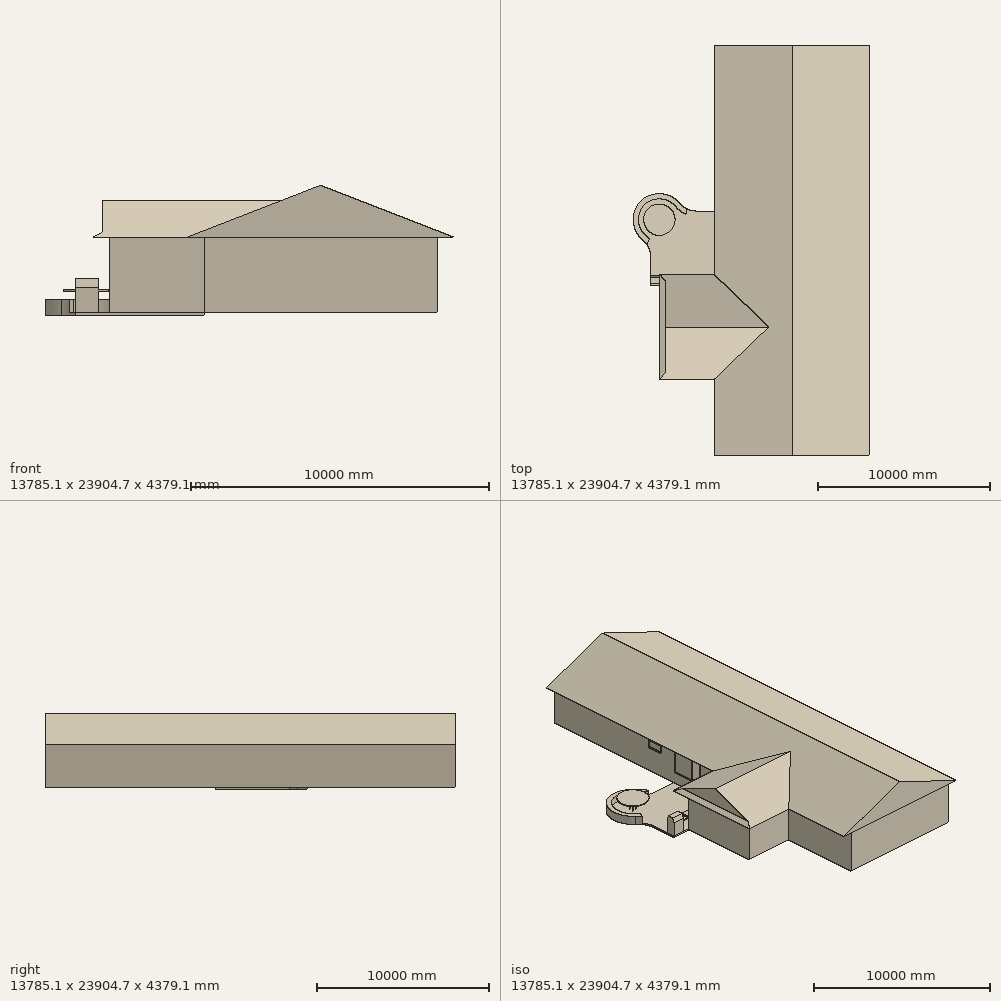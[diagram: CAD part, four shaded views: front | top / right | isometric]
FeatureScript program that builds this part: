
annotation { "Feature Type Name" : "Feature", "Feature Type Description" : "" }
export const myFeature = defineFeature(function(context is Context, id is Id, definition is map)
    precondition{}
    {
        {
            var Q0;
            Q0=qCreatedBy(makeId("Top.planeOp"),FACE);
            var sketch = newSketch(context, id + "F0", { "sketchPlane" : qUnion([Q0])});
            skLineSegment(sketch, "E0", {"start": v(0, 0) * mm, "end": v(-3175, 0) * mm});
            skLineSegment(sketch, "E1", {"start": v(-3175, 0) * mm, "end": v(-3175, -4902.2) * mm});
            skLineSegment(sketch, "E2", {"start": v(-3175, -4902.2) * mm, "end": v(0, -4902.2) * mm});
            skLineSegment(sketch, "E3", {"start": v(0, -4902.2) * mm, "end": v(0, -9934.69) * mm});
            skLineSegment(sketch, "E4", {"start": v(0, -9934.69) * mm, "end": v(7841.53, -9934.69) * mm});
            skLineSegment(sketch, "E5", {"start": v(7841.53, -9934.69) * mm, "end": v(7841.53, 13970) * mm});
            skLineSegment(sketch, "E6", {"start": v(7841.53, 13970) * mm, "end": v(0, 13970) * mm});
            skLineSegment(sketch, "E7", {"start": v(0, 13970) * mm, "end": v(0, 0) * mm});
            skSolve(sketch);
        }
        {
            var Q0;
            Q0 = qSketchRegion(id + "F0", true);
            extrude(context, id + "F1", {"entities" : qUnion([Q0]), "depth" : 2514.6 * mm, "offsetDistance" : 25.4 * mm});
        }
        {
            var Q0;
            Q0=qCreatedBy(makeId("Front.planeOp"),FACE);
            var sketch = newSketch(context, id + "F2", { "sketchPlane" : qUnion([Q0])});
            skLineSegment(sketch, "E8", {"start": v(8451.13, 2514.6) * mm, "end": v(-609.6, 2514.6) * mm});
            skLineSegment(sketch, "E9", {"start": v(-609.6, 2514.6) * mm, "end": v(3920.77, 4277.52) * mm});
            skLineSegment(sketch, "E10", {"start": v(3920.77, 4277.52) * mm, "end": v(8451.13, 2514.6) * mm});
            skSolve(sketch);
        }
        {
            var Q0;
            Q0=makeQuery(id+"F2.imprint","IMPRINT",FACE,{"disambiguationData":[TD([[makeQuery(id+"F2.imprint","IMPRINT",EDGE,{"derivedFrom":sQuery(id+"F2.wireOp",EDGE,"E8")}),-1.0]])]});
            var Q1;
            Q1=makeQuery(id+"F1.opExtrude","SWEPT_FACE",FACE,{"disambiguationData":[OSD([sQuery(id+"F0.wireOp",EDGE,"E6")])]});
            var Q2;
            Q2=makeQuery(id+"F1.opExtrude","SWEPT_FACE",FACE,{"disambiguationData":[OSD([sQuery(id+"F0.wireOp",EDGE,"E4")])]});
            extrude(context, id + "F3", {"entities" : qUnion([Q0]), "endBound" : BoundingType.UP_TO_SURFACE, "oppositeDirection" : true, "depth" : 25.4 * mm, "endBoundEntityFace" : qUnion([Q1]), "offsetDistance" : 25.4 * mm, "hasSecondDirection" : true, "secondDirectionBound" : SecondDirectionBoundingType.UP_TO_SURFACE, "secondDirectionOppositeDirection" : false, "secondDirectionDepth" : 25.4 * mm, "secondDirectionBoundEntityFace" : qUnion([Q2])});
        }
        {
            var Q0;
            Q0=makeQuery(id+"F1.opExtrude","SWEPT_FACE",FACE,{"disambiguationData":[OSD([sQuery(id+"F0.wireOp",EDGE,"E1")])]});
            var sketch = newSketch(context, id + "F4", { "sketchPlane" : qUnion([Q0])});
            skLineSegment(sketch, "E11", {"start": v(-609.6, 2514.6) * mm, "end": v(5511.8, 2514.6) * mm});
            skLineSegment(sketch, "E12", {"start": v(5511.8, 2514.6) * mm, "end": v(2451.1, 3758.26) * mm});
            skLineSegment(sketch, "E13", {"start": v(2451.1, 3758.26) * mm, "end": v(-609.6, 2514.6) * mm});
            skSolve(sketch);
        }
        {
            var Q0;
            {var subQ0=sQuery(id+"F4.wireOp",EDGE,"E12");Q0=makeQuery(id+"F4.imprint","IMPRINT",FACE,{"disambiguationData":[TD([[makeQuery(id+"F4.imprint","IMPRINT",EDGE,{"derivedFrom":subQ0}),1.0]])]});}
            extrude(context, id + "F5", {"entities" : qUnion([Q0]), "endBound" : BoundingType.UP_TO_NEXT, "oppositeDirection" : true, "depth" : 25.4 * mm, "offsetDistance" : 25.4 * mm, "hasSecondDirection" : true, "secondDirectionOppositeDirection" : false, "secondDirectionDepth" : 254 * mm});
        }
        {
            var Q0;
            Q0=makeQuery(id+"F1.opExtrude","SWEPT_FACE",FACE,{"disambiguationData":[OSD([sQuery(id+"F0.wireOp",EDGE,"E0")])]});
            var sketch = newSketch(context, id + "F6", { "sketchPlane" : qUnion([Q0])});
            skLineSegment(sketch, "E14", {"start": v(3429, 2514.6) * mm, "end": v(3784.6, 2514.6) * mm});
            skLineSegment(sketch, "E15", {"start": v(3784.6, 2514.6) * mm, "end": v(3429, 2682.87) * mm});
            skLineSegment(sketch, "E16", {"start": v(3429, 2682.87) * mm, "end": v(3429, 2514.6) * mm});
            skSolve(sketch);
        }
        {
            var Q0;
            Q0=makeQuery(id+"F6.imprint","IMPRINT",FACE,{"disambiguationData":[TD([[makeQuery(id+"F6.imprint","IMPRINT",EDGE,{"derivedFrom":sQuery(id+"F6.wireOp",EDGE,"E14")}),1.0]])]});
            var Q1;
            Q1=makeQuery(id+"F5.opExtrude","SWEPT_FACE",FACE,{"disambiguationData":[OSD([sQuery(id+"F4.wireOp",EDGE,"E13")])]});
            var Q2;
            Q2=makeQuery(id+"F5.opExtrude","SWEPT_FACE",FACE,{"disambiguationData":[OSD([sQuery(id+"F4.wireOp",EDGE,"E12")])]});
            extrude(context, id + "F7", {"entities" : qUnion([Q0]), "operationType" : NewBodyOperationType.ADD, "endBound" : BoundingType.UP_TO_SURFACE, "depth" : 25.4 * mm, "endBoundEntityFace" : qUnion([Q1]), "offsetDistance" : 25.4 * mm, "hasSecondDirection" : true, "secondDirectionBound" : SecondDirectionBoundingType.UP_TO_SURFACE, "secondDirectionOppositeDirection" : true, "secondDirectionDepth" : 25.4 * mm, "secondDirectionBoundEntityFace" : qUnion([Q2])});
        }
        {
            var Q0;
            Q0=makeQuery(id+"F1.opExtrude","SWEPT_FACE",FACE,{"disambiguationData":[OSD([sQuery(id+"F0.wireOp",EDGE,"E0")])]});
            var sketch = newSketch(context, id + "F8", { "sketchPlane" : qUnion([Q0])});
            skLineSegment(sketch, "E17.bottom", {"start": v(660.4, 2235.2) * mm, "end": v(2463.8, 2235.2) * mm});
            skLineSegment(sketch, "E17.top", {"start": v(660.4, 228.6) * mm, "end": v(2463.8, 228.6) * mm});
            skLineSegment(sketch, "E17.left", {"start": v(660.4, 2235.2) * mm, "end": v(660.4, 228.6) * mm});
            skLineSegment(sketch, "E18.right", {"start": v(2463.8, 2235.2) * mm, "end": v(2463.8, 228.6) * mm});
            skLineSegment(sketch, "E19.0", {"start": v(711.2, 2184.4) * mm, "end": v(1536.7, 2184.4) * mm});
            skLineSegment(sketch, "E19.1", {"start": v(711.2, 2184.4) * mm, "end": v(711.2, 279.4) * mm});
            skLineSegment(sketch, "E19.2", {"start": v(711.2, 279.4) * mm, "end": v(1536.7, 279.4) * mm});
            skLineSegment(sketch, "E19.3", {"start": v(1536.7, 2184.4) * mm, "end": v(1536.7, 279.4) * mm});
            skLineSegment(sketch, "E20.0", {"start": v(-6.35, -6.35) * mm, "end": v(3181.35, -6.35) * mm});
            skLineSegment(sketch, "E20.1", {"start": v(-6.35, 2520.95) * mm, "end": v(-6.35, -6.35) * mm});
            skLineSegment(sketch, "E20.2", {"start": v(3181.35, 2520.95) * mm, "end": v(-6.35, 2520.95) * mm});
            skLineSegment(sketch, "E20.3", {"start": v(3181.35, -6.35) * mm, "end": v(3181.35, 2520.95) * mm});
            skLineSegment(sketch, "E21.0", {"start": v(1587.5, 2184.4) * mm, "end": v(2413, 2184.4) * mm});
            skLineSegment(sketch, "E21.1", {"start": v(1587.5, 2184.4) * mm, "end": v(1587.5, 279.4) * mm});
            skLineSegment(sketch, "E21.2", {"start": v(1587.5, 279.4) * mm, "end": v(2413, 279.4) * mm});
            skLineSegment(sketch, "E21.3", {"start": v(2413, 2184.4) * mm, "end": v(2413, 279.4) * mm});
            skLineSegment(sketch, "E22", {"start": v(1562.1, 2298.82) * mm, "end": v(1562.1, -195.7) * mm, "construction": true});
            skSolve(sketch);
        }
        {
            var Q0;
            Q0=makeQuery(id+"F8.imprint","IMPRINT",FACE,{"disambiguationData":[TD([[makeQuery(id+"F8.imprint","IMPRINT",EDGE,{"derivedFrom":sQuery(id+"F8.wireOp",EDGE,"E17.bottom")}),-1.0]])]});
            var Q1;
            Q1=makeQuery(id+"F8.imprint","IMPRINT",FACE,{"disambiguationData":[TD([[makeQuery(id+"F8.imprint","IMPRINT",EDGE,{"derivedFrom":sQuery(id+"F8.wireOp",EDGE,"E18.bottom")}),-1.0]])]});
            extrude(context, id + "F9", {"entities" : qUnion([Q0, Q1]), "depth" : 25.4 * mm, "offsetDistance" : 25.4 * mm});
        }
        {
            var Q0;
            Q0=makeQuery(id+"F1.opExtrude","SWEPT_FACE",FACE,{"disambiguationData":[OSD([sQuery(id+"F0.wireOp",EDGE,"E0")])]});
            var sketch = newSketch(context, id + "F10", { "sketchPlane" : qUnion([Q0])});
            skLineSegment(sketch, "E23.0", {"start": v(711.2, 2184.4) * mm, "end": v(711.2, 279.4) * mm});
            skLineSegment(sketch, "E24.0", {"start": v(711.2, 2184.4) * mm, "end": v(1536.7, 2184.4) * mm});
            skLineSegment(sketch, "E25.0", {"start": v(1536.7, 2184.4) * mm, "end": v(1536.7, 279.4) * mm});
            skLineSegment(sketch, "E26.0", {"start": v(711.2, 279.4) * mm, "end": v(1536.7, 279.4) * mm});
            skLineSegment(sketch, "E27.0", {"start": v(1587.5, 2184.4) * mm, "end": v(1587.5, 279.4) * mm});
            skPoint(sketch, "E28.0", {"position": v(2000.25, 279.4) * mm});
            skLineSegment(sketch, "E29.0", {"start": v(2413, 2184.4) * mm, "end": v(2413, 279.4) * mm});
            skLineSegment(sketch, "E30.0", {"start": v(1587.5, 2184.4) * mm, "end": v(2413, 2184.4) * mm});
            skLineSegment(sketch, "E31", {"start": v(1587.5, 279.4) * mm, "end": v(2413, 279.4) * mm});
            skSolve(sketch);
        }
        {
            var Q0;
            Q0 = qSketchRegion(id + "F10", true);
            extrude(context, id + "F11", {"entities" : qUnion([Q0]), "depth" : 12.7 * mm, "offsetDistance" : 25.4 * mm});
        }
        {
            var Q0;
            Q0=makeQuery(id+"F1.opExtrude","SWEPT_FACE",FACE,{"disambiguationData":[OSD([sQuery(id+"F0.wireOp",EDGE,"E7")])]});
            var sketch = newSketch(context, id + "F12", { "sketchPlane" : qUnion([Q0])});
            skLineSegment(sketch, "E32.bottom", {"start": v(-1193.8, 2514.6) * mm, "end": v(-304.8, 2514.6) * mm});
            skLineSegment(sketch, "E32.top", {"start": v(-1193.8, 990.6) * mm, "end": v(-304.8, 990.6) * mm});
            skLineSegment(sketch, "E32.left", {"start": v(-1193.8, 2514.6) * mm, "end": v(-1193.8, 990.6) * mm});
            skLineSegment(sketch, "E32.right", {"start": v(-304.8, 2514.6) * mm, "end": v(-304.8, 990.6) * mm});
            skLineSegment(sketch, "E33.0", {"start": v(-1143, 2463.8) * mm, "end": v(-355.6, 2463.8) * mm});
            skLineSegment(sketch, "E33.1", {"start": v(-1143, 2463.8) * mm, "end": v(-1143, 1041.4) * mm});
            skLineSegment(sketch, "E33.2", {"start": v(-1143, 1041.4) * mm, "end": v(-355.6, 1041.4) * mm});
            skLineSegment(sketch, "E33.3", {"start": v(-355.6, 2463.8) * mm, "end": v(-355.6, 1041.4) * mm});
            skLineSegment(sketch, "E34.0", {"start": v(-13976.35, -6.35) * mm, "end": v(6.35, -6.35) * mm});
            skLineSegment(sketch, "E34.1", {"start": v(-13976.35, 2520.95) * mm, "end": v(-13976.35, -6.35) * mm});
            skLineSegment(sketch, "E34.2", {"start": v(6.35, 2520.95) * mm, "end": v(-13976.35, 2520.95) * mm});
            skLineSegment(sketch, "E34.3", {"start": v(6.35, -6.35) * mm, "end": v(6.35, 2520.95) * mm});
            skSolve(sketch);
        }
        {
            var Q0;
            Q0=makeQuery(id+"F12.imprint","IMPRINT",FACE,{"disambiguationData":[TD([[makeQuery(id+"F12.imprint","IMPRINT",EDGE,{"derivedFrom":sQuery(id+"F12.wireOp",EDGE,"E32.bottom")}),-1.0]])]});
            extrude(context, id + "F13", {"entities" : qUnion([Q0]), "depth" : 25.4 * mm, "offsetDistance" : 25.4 * mm});
        }
        {
            var Q0;
            Q0=makeQuery(id+"F1.opExtrude","SWEPT_FACE",FACE,{"disambiguationData":[OSD([sQuery(id+"F0.wireOp",EDGE,"E7")])]});
            var sketch = newSketch(context, id + "F14", { "sketchPlane" : qUnion([Q0])});
            skLineSegment(sketch, "E35.0", {"start": v(-355.6, 2463.8) * mm, "end": v(-355.6, 1041.4) * mm});
            skLineSegment(sketch, "E36.0", {"start": v(-1143, 2463.8) * mm, "end": v(-355.6, 2463.8) * mm});
            skLineSegment(sketch, "E37.0", {"start": v(-1143, 2463.8) * mm, "end": v(-1143, 1041.4) * mm});
            skLineSegment(sketch, "E38.0", {"start": v(-1143, 1041.4) * mm, "end": v(-355.6, 1041.4) * mm});
            skSolve(sketch);
        }
        {
            var Q0;
            Q0 = qSketchRegion(id + "F14", true);
            extrude(context, id + "F15", {"entities" : qUnion([Q0]), "depth" : 6.35 * mm, "offsetDistance" : 25.4 * mm});
        }
        {
            var Q0;
            Q0=makeQuery(id+"F3.opExtrude","SWEPT_FACE",FACE,{"disambiguationData":[OSD([sQuery(id+"F2.wireOp",EDGE,"E8")])]});
            var sketch = newSketch(context, id + "F16", { "sketchPlane" : qUnion([Q0])});
            skLineSegment(sketch, "E39", {"start": v(0, -2235.2) * mm, "end": v(0, -4089.4) * mm});
            skLineSegment(sketch, "E40", {"start": v(0, -4089.4) * mm, "end": v(-431.8, -3860.8) * mm});
            skLineSegment(sketch, "E41", {"start": v(-431.8, -3860.8) * mm, "end": v(-431.8, -2463.8) * mm});
            skLineSegment(sketch, "E42", {"start": v(-431.8, -2463.8) * mm, "end": v(0, -2235.2) * mm});
            skLineSegment(sketch, "E43", {"start": v(-431.8, -3162.3) * mm, "end": v(358.3, -3162.3) * mm, "construction": true});
            skSolve(sketch);
        }
        {
            var Q0;
            Q0=makeQuery(id+"F16.imprint","IMPRINT",FACE,{"disambiguationData":[TD([[makeQuery(id+"F16.imprint","IMPRINT",EDGE,{"derivedFrom":sQuery(id+"F16.wireOp",EDGE,"E39")}),-1.0]])]});
            extrude(context, id + "F17", {"entities" : qUnion([Q0]), "depth" : 1473.2 * mm, "offsetDistance" : 25.4 * mm});
        }
        {
            var Q0;
            Q0=makeQuery(id+"F17.opExtrude","SWEPT_FACE",FACE,{"disambiguationData":[OSD([sQuery(id+"F16.wireOp",EDGE,"E40")])]});
            var sketch = newSketch(context, id + "F18", { "sketchPlane" : qUnion([Q0])});
            skLineSegment(sketch, "E44.0", {"start": v(-1475.6, 2463.8) * mm, "end": v(-1862.58, 2463.8) * mm});
            skLineSegment(sketch, "E44.1", {"start": v(-1475.6, 1092.2) * mm, "end": v(-1475.6, 2463.8) * mm});
            skLineSegment(sketch, "E44.2", {"start": v(-1862.58, 1092.2) * mm, "end": v(-1475.6, 1092.2) * mm});
            skLineSegment(sketch, "E44.3", {"start": v(-1862.58, 2463.8) * mm, "end": v(-1862.58, 1092.2) * mm});
            skSolve(sketch);
        }
        {
            var Q0;
            Q0 = qSketchRegion(id + "F18", true);
            extrude(context, id + "F19", {"entities" : qUnion([Q0]), "operationType" : NewBodyOperationType.REMOVE, "oppositeDirection" : true, "depth" : 25.4 * mm, "offsetDistance" : 25.4 * mm});
        }
        {
            var Q0;
            Q0=makeQuery(id+"F17.opExtrude","SWEPT_FACE",FACE,{"disambiguationData":[OSD([sQuery(id+"F16.wireOp",EDGE,"E41")])]});
            var sketch = newSketch(context, id + "F20", { "sketchPlane" : qUnion([Q0])});
            skLineSegment(sketch, "E45.0", {"start": v(-2514.6, 2463.8) * mm, "end": v(-3810, 2463.8) * mm});
            skLineSegment(sketch, "E45.1", {"start": v(-2514.6, 1092.2) * mm, "end": v(-2514.6, 2463.8) * mm});
            skLineSegment(sketch, "E45.2", {"start": v(-3810, 1092.2) * mm, "end": v(-2514.6, 1092.2) * mm});
            skLineSegment(sketch, "E45.3", {"start": v(-3810, 2463.8) * mm, "end": v(-3810, 1092.2) * mm});
            skSolve(sketch);
        }
        {
            var Q0;
            Q0=makeQuery(id+"F20.imprint","IMPRINT",FACE,{"disambiguationData":[TD([[makeQuery(id+"F20.imprint","IMPRINT",EDGE,{"derivedFrom":sQuery(id+"F20.wireOp",EDGE,"E45.0")}),1.0]])]});
            extrude(context, id + "F21", {"entities" : qUnion([Q0]), "operationType" : NewBodyOperationType.REMOVE, "oppositeDirection" : true, "depth" : 25.4 * mm, "offsetDistance" : 25.4 * mm});
        }
        {
            var Q0;
            Q0=makeQuery(id+"F17.opExtrude","SWEPT_FACE",FACE,{"disambiguationData":[OSD([sQuery(id+"F16.wireOp",EDGE,"E42")])]});
            var sketch = newSketch(context, id + "F22", { "sketchPlane" : qUnion([Q0])});
            skLineSegment(sketch, "E46.0", {"start": v(-1096.62, 2463.8) * mm, "end": v(-1483.6, 2463.8) * mm});
            skLineSegment(sketch, "E46.1", {"start": v(-1096.62, 1092.2) * mm, "end": v(-1096.62, 2463.8) * mm});
            skLineSegment(sketch, "E46.2", {"start": v(-1483.6, 1092.2) * mm, "end": v(-1096.62, 1092.2) * mm});
            skLineSegment(sketch, "E46.3", {"start": v(-1483.6, 2463.8) * mm, "end": v(-1483.6, 1092.2) * mm});
            skSolve(sketch);
        }
        {
            var Q0;
            Q0 = qSketchRegion(id + "F22", true);
            extrude(context, id + "F23", {"entities" : qUnion([Q0]), "operationType" : NewBodyOperationType.REMOVE, "oppositeDirection" : true, "depth" : 25.4 * mm, "offsetDistance" : 25.4 * mm});
        }
        {
            var Q0;
            Q0=makeQuery(id+"F19.boolean.opBoolean","COPY",FACE,{"derivedFrom":makeQuery(id+"F19.opExtrude","CAP_FACE",FACE,{"disambiguationData":[OSD([sQuery(id+"F18.wireOp",EDGE,"E44.0"),sQuery(id+"F18.wireOp",EDGE,"E44.1"),sQuery(id+"F18.wireOp",EDGE,"E44.2"),sQuery(id+"F18.wireOp",EDGE,"E44.3")])],"isStart":false})});
            extrude(context, id + "F24", {"entities" : qUnion([Q0]), "depth" : 6.35 * mm, "offsetDistance" : 25.4 * mm});
        }
        {
            var Q0;
            Q0=makeQuery(id+"F21.boolean.opBoolean","COPY",FACE,{"derivedFrom":makeQuery(id+"F21.opExtrude","CAP_FACE",FACE,{"disambiguationData":[OSD([sQuery(id+"F20.wireOp",EDGE,"E45.0"),sQuery(id+"F20.wireOp",EDGE,"E45.1"),sQuery(id+"F20.wireOp",EDGE,"E45.2"),sQuery(id+"F20.wireOp",EDGE,"E45.3")])],"isStart":false})});
            extrude(context, id + "F25", {"entities" : qUnion([Q0]), "depth" : 6.35 * mm, "offsetDistance" : 25.4 * mm});
        }
        {
            var Q0;
            Q0=makeQuery(id+"F23.boolean.opBoolean","COPY",FACE,{"derivedFrom":makeQuery(id+"F23.opExtrude","CAP_FACE",FACE,{"disambiguationData":[OSD([sQuery(id+"F22.wireOp",EDGE,"E46.0"),sQuery(id+"F22.wireOp",EDGE,"E46.1"),sQuery(id+"F22.wireOp",EDGE,"E46.2"),sQuery(id+"F22.wireOp",EDGE,"E46.3")])],"isStart":false})});
            extrude(context, id + "F26", {"entities" : qUnion([Q0]), "depth" : 6.35 * mm, "offsetDistance" : 25.4 * mm});
        }
        {
            var Q0;
            Q0=makeQuery(id+"F1.opExtrude","SWEPT_FACE",FACE,{"disambiguationData":[OSD([sQuery(id+"F0.wireOp",EDGE,"E7")])]});
            var sketch = newSketch(context, id + "F27", { "sketchPlane" : qUnion([Q0])});
            skLineSegment(sketch, "E47.bottom", {"start": v(-6197.6, 50.8) * mm, "end": v(-5181.6, 50.8) * mm});
            skLineSegment(sketch, "E47.top", {"start": v(-6197.6, 0) * mm, "end": v(-5181.6, 0) * mm});
            skLineSegment(sketch, "E47.left", {"start": v(-6197.6, 50.8) * mm, "end": v(-6197.6, 0) * mm});
            skLineSegment(sketch, "E47.right", {"start": v(-5181.6, 50.8) * mm, "end": v(-5181.6, 0) * mm});
            skSolve(sketch);
        }
        {
            var Q0;
            Q0=makeQuery(id+"F27.imprint","IMPRINT",FACE,{"disambiguationData":[TD([[makeQuery(id+"F27.imprint","IMPRINT",EDGE,{"derivedFrom":sQuery(id+"F27.wireOp",EDGE,"E47.bottom")}),1.0]])]});
            var sketch = newSketch(context, id + "F28", { "sketchPlane" : qUnion([Q0])});
            skLineSegment(sketch, "E48.bottom", {"start": v(-6324.6, 2514.6) * mm, "end": v(-5359.4, 2514.6) * mm});
            skLineSegment(sketch, "E48.top", {"start": v(-6324.6, 1498.6) * mm, "end": v(-5359.4, 1498.6) * mm});
            skLineSegment(sketch, "E48.left", {"start": v(-6324.6, 2514.6) * mm, "end": v(-6324.6, 1498.6) * mm});
            skLineSegment(sketch, "E48.right", {"start": v(-5359.4, 2514.6) * mm, "end": v(-5359.4, 1498.6) * mm});
            skPoint(sketch, "E49", {"position": v(-9266.52, 0) * mm});
            skLineSegment(sketch, "E50.bottom", {"start": v(-6264.92, 2466.6) * mm, "end": v(-5423.94, 2466.6) * mm});
            skLineSegment(sketch, "E50.top", {"start": v(-6264.92, 2033.98) * mm, "end": v(-5423.94, 2033.98) * mm});
            skLineSegment(sketch, "E50.left", {"start": v(-6264.92, 2466.6) * mm, "end": v(-6264.92, 2033.98) * mm});
            skLineSegment(sketch, "E50.right", {"start": v(-5423.94, 2466.6) * mm, "end": v(-5423.94, 2033.98) * mm});
            skLineSegment(sketch, "E51.bottom", {"start": v(-6268.96, 1969.29) * mm, "end": v(-5427.98, 1969.29) * mm});
            skLineSegment(sketch, "E51.top", {"start": v(-6268.96, 1564.97) * mm, "end": v(-5427.98, 1564.97) * mm});
            skLineSegment(sketch, "E51.left", {"start": v(-6268.96, 1969.29) * mm, "end": v(-6268.96, 1564.97) * mm});
            skLineSegment(sketch, "E51.right", {"start": v(-5427.98, 1969.29) * mm, "end": v(-5427.98, 1564.97) * mm});
            skSolve(sketch);
        }
        {
            var Q0;
            Q0=makeQuery(id+"F28.imprint","IMPRINT",FACE,{"disambiguationData":[TD([[makeQuery(id+"F28.imprint","IMPRINT",EDGE,{"derivedFrom":sQuery(id+"F28.wireOp",EDGE,"E48.bottom")}),-1.0]])]});
            extrude(context, id + "F29", {"entities" : qUnion([Q0]), "depth" : 25.4 * mm, "offsetDistance" : 25.4 * mm});
        }
        {
            var Q0;
            Q0=makeQuery(id+"F27.imprint","IMPRINT",FACE,{"disambiguationData":[TD([[makeQuery(id+"F27.imprint","IMPRINT",EDGE,{"derivedFrom":sQuery(id+"F27.wireOp",EDGE,"E47.bottom")}),1.0]])]});
            var sketch = newSketch(context, id + "F30", { "sketchPlane" : qUnion([Q0])});
            skLineSegment(sketch, "E52.bottom", {"start": v(-6265.82, 2468.48) * mm, "end": v(-5422, 2468.48) * mm});
            skLineSegment(sketch, "E52.top", {"start": v(-6265.82, 2028.54) * mm, "end": v(-5422, 2028.54) * mm});
            skLineSegment(sketch, "E52.left", {"start": v(-6265.82, 2468.48) * mm, "end": v(-6265.82, 2028.54) * mm});
            skLineSegment(sketch, "E52.right", {"start": v(-5422, 2468.48) * mm, "end": v(-5422, 2028.54) * mm});
            skLineSegment(sketch, "E53.bottom", {"start": v(-6268.23, 1970.84) * mm, "end": v(-5426.8, 1970.84) * mm});
            skLineSegment(sketch, "E53.top", {"start": v(-6268.23, 1564.55) * mm, "end": v(-5426.8, 1564.55) * mm});
            skLineSegment(sketch, "E53.left", {"start": v(-6268.23, 1970.84) * mm, "end": v(-6268.23, 1564.55) * mm});
            skLineSegment(sketch, "E53.right", {"start": v(-5426.8, 1970.84) * mm, "end": v(-5426.8, 1564.55) * mm});
            skPoint(sketch, "E54.0.3.end.orphan", {"position": v(-5359.4, 1498.6) * mm});
            skPoint(sketch, "E54.0.1.start.orphan", {"position": v(-5359.4, 2514.6) * mm});
            skPoint(sketch, "E54.0.2.end.orphan", {"position": v(-6324.6, 1498.6) * mm});
            skPoint(sketch, "E54.0.2.start.orphan", {"position": v(-6324.6, 2514.6) * mm});
            skSolve(sketch);
        }
        {
            var Q0;
            Q0=makeQuery(id+"F30.imprint","IMPRINT",FACE,{"disambiguationData":[TD([[makeQuery(id+"F30.imprint","IMPRINT",EDGE,{"derivedFrom":sQuery(id+"F30.wireOp",EDGE,"E52.bottom")}),-1.0]])]});
            var Q1;
            Q1=makeQuery(id+"F30.imprint","IMPRINT",FACE,{"disambiguationData":[TD([[makeQuery(id+"F30.imprint","IMPRINT",EDGE,{"derivedFrom":sQuery(id+"F30.wireOp",EDGE,"E53.bottom")}),-1.0]])]});
            extrude(context, id + "F31", {"entities" : qUnion([Q0, Q1]), "depth" : 6.35 * mm, "offsetDistance" : 25.4 * mm});
        }
        {
            var Q0;
            Q0=qCreatedBy(makeId("Top.planeOp"),FACE);
            var sketch = newSketch(context, id + "F32", { "sketchPlane" : qUnion([Q0])});
            skLineSegment(sketch, "E55.bottom", {"start": v(0, 0) * mm, "end": v(-4318, 0) * mm});
            skLineSegment(sketch, "E55.top", {"start": v(0, 4318) * mm, "end": v(-1654.74, 4318) * mm});
            skLineSegment(sketch, "E55.left", {"start": v(0, 0) * mm, "end": v(0, 4318) * mm});
            skLineSegment(sketch, "E55.right", {"start": v(-4318, 0) * mm, "end": v(-4318, 1654.74) * mm});
            skArc(sketch, "E56", {"start": v(-2634.4, 4779.82) * mm, "mid": v(-4887.63, 4887.63) * mm, "end": v(-4779.82, 2634.4) * mm});
            skArc(sketch, "E57.filletArc", {"start": v(-2634.4, 4779.82) * mm, "mid": v(-2196.27, 4439.24) * mm, "end": v(-1654.74, 4318) * mm});
            skArc(sketch, "E58.filletArc", {"start": v(-4318, 1654.74) * mm, "mid": v(-4439.24, 2196.27) * mm, "end": v(-4779.82, 2634.4) * mm});
            skSolve(sketch);
        }
        {
            var Q0;
            Q0=makeQuery(id+"F32.imprint","IMPRINT",FACE,{"disambiguationData":[TD([[makeQuery(id+"F32.imprint","IMPRINT",EDGE,{"derivedFrom":sQuery(id+"F32.wireOp",EDGE,"E55.bottom")}),-1.0]])]});
            extrude(context, id + "F33", {"entities" : qUnion([Q0]), "oppositeDirection" : true, "depth" : 101.6 * mm, "offsetDistance" : 25.4 * mm});
        }
        {
            var Q0;
            Q0=makeQuery(id+"F27.imprint","IMPRINT",FACE,{"disambiguationData":[TD([[makeQuery(id+"F27.imprint","IMPRINT",EDGE,{"derivedFrom":sQuery(id+"F27.wireOp",EDGE,"E47.bottom")}),1.0]])]});
            var Q1;
            Q1=sQuery(id+"F32.wireOp",VERTEX,"E56.center");
            cPlane(context, id + "F34", {"entities" : qUnion([Q0, Q1]), "cplaneType" : CPlaneType.PLANE_POINT, "offset" : 3048 * mm, "width" : 152.4 * mm, "height" : 152.4 * mm});
        }
        {
            var Q0;
            Q0=makeQuery(id+"F1.opExtrude","SWEPT_FACE",FACE,{"disambiguationData":[OSD([sQuery(id+"F0.wireOp",EDGE,"E0")])]});
            var Q1;
            Q1=sQuery(id+"F32.wireOp",VERTEX,"E56.center");
            cPlane(context, id + "F35", {"entities" : qUnion([Q0, Q1]), "cplaneType" : CPlaneType.PLANE_POINT, "offset" : 2921 * mm, "width" : 152.4 * mm, "height" : 152.4 * mm});
        }
        {
            var Q0;
            Q0=makeQuery(id+"F33.opExtrude","CAP_FACE",FACE,{"disambiguationData":[OSD([sQuery(id+"F32.wireOp",EDGE,"E55.bottom"),sQuery(id+"F32.wireOp",EDGE,"E55.top"),sQuery(id+"F32.wireOp",EDGE,"E55.left"),sQuery(id+"F32.wireOp",EDGE,"E55.right"),sQuery(id+"F32.wireOp",EDGE,"c891b3c9-2984-49ea-b5f4-79698e13750f.filletArc")])],"isStart":true});
            var sketch = newSketch(context, id + "F36", { "sketchPlane" : qUnion([Q0])});
            skCircle(sketch, "E59", {"center": v(-3700.42, 3937) * mm, "radius": 38.1 * mm});
            skCircle(sketch, "E60", {"center": v(-3700.42, 3683) * mm, "radius": 38.1 * mm});
            skCircle(sketch, "E61", {"center": v(-3919.58, 3683) * mm, "radius": 38.1 * mm});
            skCircle(sketch, "E62", {"center": v(-3919.58, 3937) * mm, "radius": 38.1 * mm});
            skLineSegment(sketch, "E63", {"start": v(-3700.42, 3937) * mm, "end": v(-3700.42, 3683) * mm, "construction": true});
            skLineSegment(sketch, "E64", {"start": v(-3700.42, 3683) * mm, "end": v(-3919.58, 3683) * mm, "construction": true});
            skLineSegment(sketch, "E65", {"start": v(-3919.58, 3937) * mm, "end": v(-3919.58, 3683) * mm, "construction": true});
            skLineSegment(sketch, "E66", {"start": v(-3700.42, 3937) * mm, "end": v(-3919.58, 3937) * mm, "construction": true});
            skLineSegment(sketch, "E67", {"start": v(-3700.42, 3937) * mm, "end": v(-3919.58, 3683) * mm, "construction": true});
            skLineSegment(sketch, "E68", {"start": v(-3700.42, 3683) * mm, "end": v(-3919.58, 3937) * mm, "construction": true});
            skPoint(sketch, "E69", {"position": v(-3810, 3810) * mm});
            skSolve(sketch);
        }
        {
            var Q0;
            Q0 = qSketchRegion(id + "F36", true);
            extrude(context, id + "F37", {"entities" : qUnion([Q0]), "depth" : 711.2 * mm, "offsetDistance" : 25.4 * mm});
        }
        {
            var Q0;
            Q0=makeQuery(id+"F37.opExtrude","CAP_FACE",FACE,{"disambiguationData":[OSD([sQuery(id+"F36.wireOp",EDGE,"E59")])],"isStart":false});
            var sketch = newSketch(context, id + "F38", { "sketchPlane" : qUnion([Q0])});
            skCircle(sketch, "E70", {"center": v(-3810, 3810) * mm, "radius": 914.4 * mm});
            skSolve(sketch);
        }
        {
            var Q0;
            Q0 = qSketchRegion(id + "F38", true);
            extrude(context, id + "F39", {"entities" : qUnion([Q0]), "operationType" : NewBodyOperationType.ADD, "depth" : 50.8 * mm, "offsetDistance" : 25.4 * mm});
        }
        {
            var Q0;
            Q0=makeQuery(id+"F32.imprint","IMPRINT",FACE,{"disambiguationData":[TD([[makeQuery(id+"F32.imprint","IMPRINT",EDGE,{"derivedFrom":sQuery(id+"F32.wireOp",EDGE,"E55.bottom")}),-1.0]])]});
            var sketch = newSketch(context, id + "F40", { "sketchPlane" : qUnion([Q0])});
            skArc(sketch, "E71.0", {"start": v(-2634.4, 4779.82) * mm, "mid": v(-4887.63, 4887.63) * mm, "end": v(-4779.82, 2634.4) * mm});
            skArc(sketch, "E72.0", {"start": v(-2634.4, 4779.82) * mm, "mid": v(-2449.2, 4597.17) * mm, "end": v(-2230.66, 4456.1) * mm});
            skArc(sketch, "E73.0", {"start": v(-4531.15, 2358.99) * mm, "mid": v(-4645.37, 2505.83) * mm, "end": v(-4779.82, 2634.4) * mm});
            skArc(sketch, "E74.0", {"start": v(-2830.64, 4536.16) * mm, "mid": v(-4715.03, 4626.93) * mm, "end": v(-4432.42, 2761.65) * mm});
            skArc(sketch, "E75.0", {"start": v(-2919.74, 4650.05) * mm, "mid": v(-2613.91, 4339) * mm, "end": v(-2234.49, 4123.8) * mm});
            skArc(sketch, "E76.0", {"start": v(-4377.1, 2661.57) * mm, "mid": v(-4565.71, 2852.62) * mm, "end": v(-4784.04, 3008.86) * mm});
            skLineSegment(sketch, "E77", {"start": v(-2230.66, 4456.1) * mm, "end": v(-2234.49, 4123.8) * mm});
            skPoint(sketch, "E78.orphan", {"position": v(-1654.74, 4318) * mm});
            skLineSegment(sketch, "E79", {"start": v(-4377.1, 2661.57) * mm, "end": v(-4531.15, 2358.99) * mm});
            skPoint(sketch, "E80.orphan", {"position": v(-4318, 1654.74) * mm});
            skSolve(sketch);
        }
        {
            var Q0;
            Q0 = qSketchRegion(id + "F40", true);
            extrude(context, id + "F41", {"entities" : qUnion([Q0]), "operationType" : NewBodyOperationType.ADD, "depth" : 431.8 * mm, "offsetDistance" : 25.4 * mm});
        }
        {
            var Q0;
            Q0=makeQuery(id+"F27.imprint","IMPRINT",FACE,{"disambiguationData":[TD([[makeQuery(id+"F27.imprint","IMPRINT",EDGE,{"derivedFrom":sQuery(id+"F27.wireOp",EDGE,"E47.bottom")}),1.0]])]});
            var sketch = newSketch(context, id + "F42", { "sketchPlane" : qUnion([Q0])});
            skLineSegment(sketch, "E81.bottom", {"start": v(-2286, 762) * mm, "end": v(0, 762) * mm});
            skLineSegment(sketch, "E81.top", {"start": v(-2286, 711.2) * mm, "end": v(0, 711.2) * mm});
            skLineSegment(sketch, "E81.left", {"start": v(-2286, 762) * mm, "end": v(-2286, 711.2) * mm});
            skLineSegment(sketch, "E81.right", {"start": v(0, 762) * mm, "end": v(0, 711.2) * mm});
            skSolve(sketch);
        }
        {
            var Q0;
            Q0=makeQuery(id+"F42.imprint","IMPRINT",FACE,{"disambiguationData":[TD([[makeQuery(id+"F42.imprint","IMPRINT",EDGE,{"derivedFrom":sQuery(id+"F42.wireOp",EDGE,"E81.bottom")}),-1.0]])]});
            extrude(context, id + "F43", {"entities" : qUnion([Q0]), "depth" : 609.6 * mm, "offsetDistance" : 25.4 * mm});
        }
        {
            var Q0;
            Q0=makeQuery(id+"F43.opExtrude","CAP_FACE",FACE,{"disambiguationData":[OSD([sQuery(id+"F42.wireOp",EDGE,"E81.bottom"),sQuery(id+"F42.wireOp",EDGE,"E81.top"),sQuery(id+"F42.wireOp",EDGE,"E81.left"),sQuery(id+"F42.wireOp",EDGE,"E81.right")])],"isStart":false});
            var sketch = newSketch(context, id + "F44", { "sketchPlane" : qUnion([Q0])});
            skPoint(sketch, "E82", {"position": v(-1143, 762) * mm});
            skSolve(sketch);
        }
        {
            var Q0;
            Q0=sQuery(id+"F44.wireOp",VERTEX,"E82");
            var Q1;
            Q1=makeQuery(id+"F43.opExtrude","SWEPT_FACE",FACE,{"disambiguationData":[OSD([sQuery(id+"F42.wireOp",EDGE,"E81.left")])]});
            cPlane(context, id + "F45", {"entities" : qUnion([Q0, Q1]), "cplaneType" : CPlaneType.PLANE_POINT, "offset" : 25.4 * mm, "width" : 152.4 * mm, "height" : 152.4 * mm});
        }
        {
            var Q0;
            Q0=makeQuery(id+"F43.opExtrude","SWEPT_FACE",FACE,{"disambiguationData":[OSD([sQuery(id+"F42.wireOp",EDGE,"E81.left")])]});
            cPlane(context, id + "F46", {"entities" : qUnion([Q0]), "cplaneType" : CPlaneType.OFFSET, "offset" : 152.4 * mm, "oppositeDirection" : true, "width" : 152.4 * mm, "height" : 152.4 * mm});
        }
        {
            var Q0;
            Q0=qCreatedBy(id+"F46.planeOp",FACE);
            var sketch = newSketch(context, id + "F47", { "sketchPlane" : qUnion([Q0])});
            skArc(sketch, "E83", {"start": v(380.51, 698.5) * mm, "mid": v(142.35, 541.51) * mm, "end": v(12.7, 287.43) * mm});
            skArc(sketch, "E84", {"start": v(228.43, 711.2) * mm, "mid": v(98.22, 606.05) * mm, "end": v(0, 470.54) * mm});
            skLineSegment(sketch, "E85", {"start": v(380.51, 698.5) * mm, "end": v(380.51, 711.2) * mm});
            skLineSegment(sketch, "E86", {"start": v(380.51, 711.2) * mm, "end": v(228.43, 711.2) * mm});
            skLineSegment(sketch, "E87", {"start": v(12.7, 287.43) * mm, "end": v(0, 287.43) * mm});
            skLineSegment(sketch, "E88", {"start": v(0, 287.43) * mm, "end": v(0, 470.54) * mm});
            skPoint(sketch, "E89.orphan", {"position": v(0, 164.8) * mm});
            skSolve(sketch);
        }
        {
            var Q0;
            Q0 = qSketchRegion(id + "F47", true);
            extrude(context, id + "F48", {"entities" : qUnion([Q0]), "oppositeDirection" : true, "depth" : 76.2 * mm, "offsetDistance" : 25.4 * mm});
        }
        {
            var Q0;
            Q0=makeQuery(id+"F48.opExtrude","SWEPT_BODY",BODY,{"disambiguationData":[OSD([sQuery(id+"F47.wireOp",EDGE,"E83"),sQuery(id+"F47.wireOp",EDGE,"E84"),sQuery(id+"F47.wireOp",EDGE,"E85"),sQuery(id+"F47.wireOp",EDGE,"E86"),sQuery(id+"F47.wireOp",EDGE,"E87"),sQuery(id+"F47.wireOp",EDGE,"E88")])]});
            var Q1;
            Q1=qCreatedBy(id+"F45.planeOp",FACE);
            mirror(context, id + "F49", {"entities" : qUnion([Q0]), "mirrorPlane" : qUnion([Q1])});
        }
        {
            var Q0;
            Q0=makeQuery(id+"F33.opExtrude","SWEPT_FACE",FACE,{"disambiguationData":[OSD([sQuery(id+"F32.wireOp",EDGE,"E55.right")])]});
            var sketch = newSketch(context, id + "F50", { "sketchPlane" : qUnion([Q0])});
            skLineSegment(sketch, "E90.bottom", {"start": v(0, 0) * mm, "end": v(-551.47, 0) * mm});
            skLineSegment(sketch, "E90.left", {"start": v(0, 0) * mm, "end": v(0, 849.06) * mm});
            skLineSegment(sketch, "E90.right", {"start": v(-551.47, 0) * mm, "end": v(-551.47, 849.06) * mm});
            skLineSegment(sketch, "E91", {"start": v(-551.47, 849.06) * mm, "end": v(-442.67, 1141.45) * mm});
            skLineSegment(sketch, "E92", {"start": v(-442.67, 1141.45) * mm, "end": v(-109.48, 1141.45) * mm});
            skLineSegment(sketch, "E93", {"start": v(-109.48, 1141.45) * mm, "end": v(0, 849.06) * mm});
            skSolve(sketch);
        }
        {
            var Q0;
            Q0=makeQuery(id+"F50.imprint","IMPRINT",FACE,{"disambiguationData":[TD([[makeQuery(id+"F50.imprint","IMPRINT",EDGE,{"derivedFrom":sQuery(id+"F50.wireOp",EDGE,"E90.bottom")}),-1.0]])]});
            var Q1;
            Q1=makeQuery(id+"F1.opExtrude","SWEPT_FACE",FACE,{"disambiguationData":[OSD([sQuery(id+"F0.wireOp",EDGE,"E1")])]});
            extrude(context, id + "F51", {"entities" : qUnion([Q0]), "oppositeDirection" : true, "depth" : 762 * mm, "endBoundEntityFace" : qUnion([Q1]), "offsetDistance" : 25.4 * mm});
        }
        {
            var Q0;
            Q0=makeQuery(id+"F1.opExtrude","SWEPT_FACE",FACE,{"disambiguationData":[OSD([sQuery(id+"F0.wireOp",EDGE,"E0")])]});
            var sketch = newSketch(context, id + "F52", { "sketchPlane" : qUnion([Q0])});
            skLineSegment(sketch, "E94.bottom", {"start": v(2540, 762) * mm, "end": v(3098.8, 762) * mm});
            skLineSegment(sketch, "E94.top", {"start": v(2540, 711.2) * mm, "end": v(3098.8, 711.2) * mm});
            skLineSegment(sketch, "E94.left", {"start": v(2540, 762) * mm, "end": v(2540, 711.2) * mm});
            skLineSegment(sketch, "E94.right", {"start": v(3098.8, 762) * mm, "end": v(3098.8, 711.2) * mm});
            skSolve(sketch);
        }
        {
            var Q0;
            Q0 = qSketchRegion(id + "F52", true);
            extrude(context, id + "F53", {"entities" : qUnion([Q0]), "depth" : 609.6 * mm, "offsetDistance" : 25.4 * mm});
        }
        {
            var Q0;
            Q0=makeQuery(id+"F51.opExtrude","CAP_FACE",FACE,{"disambiguationData":[OSD([sQuery(id+"F50.wireOp",EDGE,"E90.bottom"),sQuery(id+"F50.wireOp",EDGE,"E90.left"),sQuery(id+"F50.wireOp",EDGE,"E90.right"),sQuery(id+"F50.wireOp",EDGE,"E91"),sQuery(id+"F50.wireOp",EDGE,"E92"),sQuery(id+"F50.wireOp",EDGE,"E93")])],"isStart":false});
            var sketch = newSketch(context, id + "F54", { "sketchPlane" : qUnion([Q0])});
            skLineSegment(sketch, "E95.bottom", {"start": v(551.47, 761.81) * mm, "end": v(0, 761.81) * mm});
            skLineSegment(sketch, "E95.top", {"start": v(551.47, 707.42) * mm, "end": v(0, 707.42) * mm});
            skLineSegment(sketch, "E95.left", {"start": v(551.47, 761.81) * mm, "end": v(551.47, 707.42) * mm});
            skLineSegment(sketch, "E95.right", {"start": v(0, 761.81) * mm, "end": v(0, 707.42) * mm});
            skSolve(sketch);
        }
        {
            var Q0;
            Q0 = qSketchRegion(id + "F54", true);
            extrude(context, id + "F55", {"entities" : qUnion([Q0]), "operationType" : NewBodyOperationType.ADD, "depth" : 355.6 * mm, "offsetDistance" : 25.4 * mm});
        }
        {
            var Q0;
            Q0=makeQuery(id+"F53.opExtrude","SWEPT_FACE",FACE,{"disambiguationData":[OSD([sQuery(id+"F52.wireOp",EDGE,"E94.bottom")])]});
            var sketch = newSketch(context, id + "F56", { "sketchPlane" : qUnion([Q0])});
            skArc(sketch, "E96", {"start": v(-2540, 508) * mm, "mid": v(-2569.76, 579.84) * mm, "end": v(-2641.6, 609.6) * mm});
            skLineSegment(sketch, "E97", {"start": v(-2540, 508) * mm, "end": v(-2540, 609.6) * mm});
            skLineSegment(sketch, "E98", {"start": v(-2540, 609.6) * mm, "end": v(-2641.6, 609.6) * mm});
            skLineSegment(sketch, "E99", {"start": v(-3098.8, 508) * mm, "end": v(-3098.8, 609.6) * mm});
            skLineSegment(sketch, "E100", {"start": v(-3098.8, 609.6) * mm, "end": v(-2997.2, 609.6) * mm});
            skArc(sketch, "E101", {"start": v(-2997.2, 609.6) * mm, "mid": v(-3069.04, 579.84) * mm, "end": v(-3098.8, 508) * mm});
            skSolve(sketch);
        }
        {
            var Q0;
            Q0=makeQuery(id+"F56.imprint","IMPRINT",FACE,{"disambiguationData":[TD([[makeQuery(id+"F56.imprint","IMPRINT",EDGE,{"derivedFrom":sQuery(id+"F56.wireOp",EDGE,"E96")}),-1.0]])]});
            var Q1;
            Q1=makeQuery(id+"F56.imprint","IMPRINT",FACE,{"disambiguationData":[TD([[makeQuery(id+"F56.imprint","IMPRINT",EDGE,{"derivedFrom":sQuery(id+"F56.wireOp",EDGE,"E99")}),1.0]])]});
            extrude(context, id + "F57", {"entities" : qUnion([Q0, Q1]), "operationType" : NewBodyOperationType.REMOVE, "endBound" : BoundingType.UP_TO_NEXT, "oppositeDirection" : true, "depth" : 25.4 * mm, "offsetDistance" : 25.4 * mm});
        }
    });
